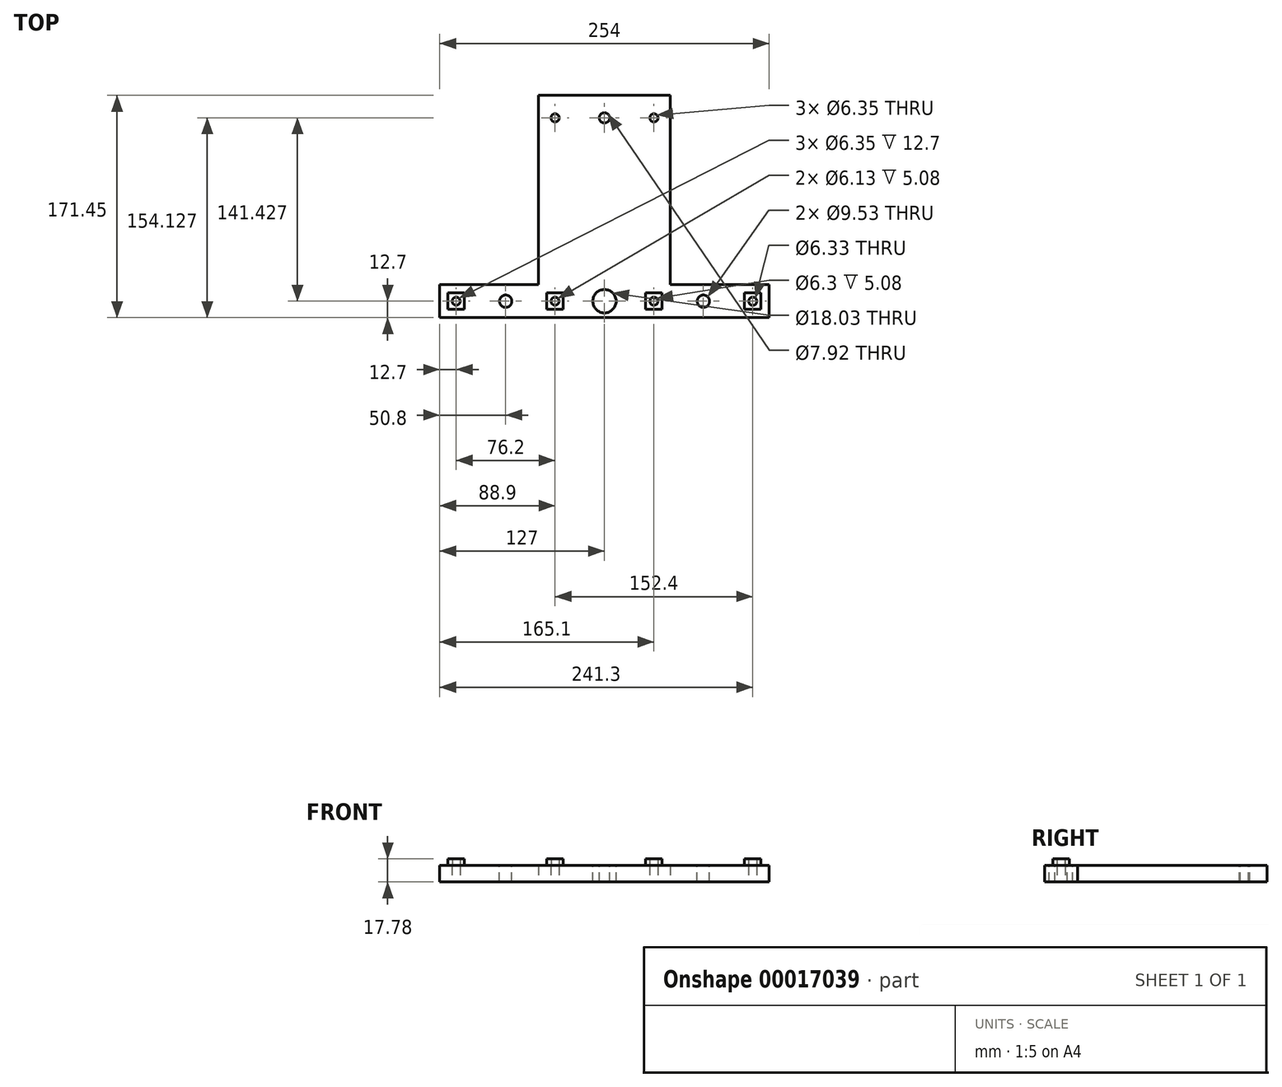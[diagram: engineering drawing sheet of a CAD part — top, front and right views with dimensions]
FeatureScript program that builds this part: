
annotation { "Feature Type Name" : "Feature", "Feature Type Description" : "" }
export const myFeature = defineFeature(function(context is Context, id is Id, definition is map)
    precondition{}
    {
        {
            var Q0;
            Q0=qCreatedBy(makeId("Top.planeOp"),FACE);
            var sketch = newSketch(context, id + "F0", { "sketchPlane" : qUnion([Q0])});
            skLineSegment(sketch, "E0.bottom", {"start": v(127, 12.7) * mm, "end": v(50.8, 12.7) * mm});
            skLineSegment(sketch, "E0.top", {"start": v(127, -12.7) * mm, "end": v(-127, -12.7) * mm});
            skLineSegment(sketch, "E0.left", {"start": v(127, 12.7) * mm, "end": v(127, -12.7) * mm});
            skLineSegment(sketch, "E0.right", {"start": v(-127, 12.7) * mm, "end": v(-127, -12.7) * mm});
            skPoint(sketch, "E0.middle", {"position": v(0, 0) * mm});
            skLineSegment(sketch, "E1.bottom", {"start": v(50.8, 158.75) * mm, "end": v(-50.8, 158.75) * mm});
            skLineSegment(sketch, "E1.top", {"start": v(50.8, -158.75) * mm, "end": v(-50.8, -158.75) * mm});
            skLineSegment(sketch, "E1.left", {"start": v(50.8, 158.75) * mm, "end": v(50.8, 12.7) * mm});
            skLineSegment(sketch, "E1.right", {"start": v(-50.8, 158.75) * mm, "end": v(-50.8, 12.7) * mm});
            skLineSegment(sketch, "E2.trimOffspring", {"start": v(-50.8, 12.7) * mm, "end": v(-127, 12.7) * mm});
            skCircle(sketch, "E3", {"center": v(114.3, 0) * mm, "radius": 3.18 * mm});
            skCircle(sketch, "E4", {"center": v(38.1, 0) * mm, "radius": 3.18 * mm});
            skCircle(sketch, "E5", {"center": v(-38.1, 0) * mm, "radius": 3.18 * mm});
            skCircle(sketch, "E6", {"center": v(-114.3, 0) * mm, "radius": 3.18 * mm});
            skSolve(sketch);
        }
        {
            var Q0;
            Q0 = qSketchRegion(id + "F0", true);
            extrude(context, id + "F1", {"entities" : qUnion([Q0]), "depth" : 12.7 * mm});
        }
        {
            var Q0;
            Q0=makeQuery(id+"F1.opExtrude","CAP_FACE",FACE,{"disambiguationData":[OSD([sQuery(id+"F0.wireOp",EDGE,"E0.bottom"),sQuery(id+"F0.wireOp",EDGE,"E0.top"),sQuery(id+"F0.wireOp",EDGE,"E0.left"),sQuery(id+"F0.wireOp",EDGE,"E0.right"),sQuery(id+"F0.wireOp",EDGE,"E1.bottom"),sQuery(id+"F0.wireOp",EDGE,"E1.left"),sQuery(id+"F0.wireOp",EDGE,"E1.right"),sQuery(id+"F0.wireOp",EDGE,"E2.trimOffspring"),sQuery(id+"F0.wireOp",EDGE,"E3"),sQuery(id+"F0.wireOp",EDGE,"E4"),sQuery(id+"F0.wireOp",EDGE,"E5"),sQuery(id+"F0.wireOp",EDGE,"E6")])],"isStart":false});
            var sketch = newSketch(context, id + "F2", { "sketchPlane" : qUnion([Q0])});
            skLineSegment(sketch, "E7.bottom", {"start": v(120.65, 6.35) * mm, "end": v(107.95, 6.35) * mm});
            skLineSegment(sketch, "E7.top", {"start": v(120.65, -6.35) * mm, "end": v(107.95, -6.35) * mm});
            skLineSegment(sketch, "E7.left", {"start": v(120.65, 6.35) * mm, "end": v(120.65, -6.35) * mm});
            skLineSegment(sketch, "E7.right", {"start": v(107.95, 6.35) * mm, "end": v(107.95, -6.35) * mm});
            skPoint(sketch, "E7.middle", {"position": v(114.3, 0) * mm});
            skLineSegment(sketch, "E8.bottom", {"start": v(44.45, 6.35) * mm, "end": v(31.75, 6.35) * mm});
            skLineSegment(sketch, "E8.top", {"start": v(44.45, -6.35) * mm, "end": v(31.75, -6.35) * mm});
            skLineSegment(sketch, "E8.left", {"start": v(44.45, 6.35) * mm, "end": v(44.45, -6.35) * mm});
            skLineSegment(sketch, "E8.right", {"start": v(31.75, 6.35) * mm, "end": v(31.75, -6.35) * mm});
            skPoint(sketch, "E8.middle", {"position": v(38.1, 0) * mm});
            skLineSegment(sketch, "E9.bottom", {"start": v(-31.75, 6.35) * mm, "end": v(-44.45, 6.35) * mm});
            skLineSegment(sketch, "E9.top", {"start": v(-31.75, -6.35) * mm, "end": v(-44.45, -6.35) * mm});
            skLineSegment(sketch, "E9.left", {"start": v(-31.75, 6.35) * mm, "end": v(-31.75, -6.35) * mm});
            skLineSegment(sketch, "E9.right", {"start": v(-44.45, 6.35) * mm, "end": v(-44.45, -6.35) * mm});
            skPoint(sketch, "E9.middle", {"position": v(-38.1, 0) * mm});
            skLineSegment(sketch, "E10.bottom", {"start": v(-107.95, 6.35) * mm, "end": v(-120.65, 6.35) * mm});
            skLineSegment(sketch, "E10.top", {"start": v(-107.95, -6.35) * mm, "end": v(-120.65, -6.35) * mm});
            skLineSegment(sketch, "E10.left", {"start": v(-107.95, 6.35) * mm, "end": v(-107.95, -6.35) * mm});
            skLineSegment(sketch, "E10.right", {"start": v(-120.65, 6.35) * mm, "end": v(-120.65, -6.35) * mm});
            skPoint(sketch, "E10.middle", {"position": v(-114.3, 0) * mm});
            skCircle(sketch, "E11", {"center": v(-114.3, 0) * mm, "radius": 3.07 * mm});
            skCircle(sketch, "E12", {"center": v(-38.1, 0) * mm, "radius": 3.07 * mm});
            skCircle(sketch, "E13", {"center": v(38.1, 0) * mm, "radius": 3.15 * mm});
            skCircle(sketch, "E14", {"center": v(114.3, 0) * mm, "radius": 3.17 * mm});
            skSolve(sketch);
        }
        {
            var Q0;
            Q0 = qSketchRegion(id + "F2", true);
            extrude(context, id + "F3", {"entities" : qUnion([Q0]), "operationType" : NewBodyOperationType.ADD, "depth" : 5.08 * mm});
        }
        {
            var Q0;
            Q0=makeQuery(id+"F1.opExtrude","CAP_FACE",FACE,{"disambiguationData":[OSD([sQuery(id+"F0.wireOp",EDGE,"E0.bottom"),sQuery(id+"F0.wireOp",EDGE,"E0.top"),sQuery(id+"F0.wireOp",EDGE,"E0.left"),sQuery(id+"F0.wireOp",EDGE,"E0.right"),sQuery(id+"F0.wireOp",EDGE,"E1.bottom"),sQuery(id+"F0.wireOp",EDGE,"E1.left"),sQuery(id+"F0.wireOp",EDGE,"E1.right"),sQuery(id+"F0.wireOp",EDGE,"E2.trimOffspring"),sQuery(id+"F0.wireOp",EDGE,"E3"),sQuery(id+"F0.wireOp",EDGE,"E4"),sQuery(id+"F0.wireOp",EDGE,"E5"),sQuery(id+"F0.wireOp",EDGE,"E6")])],"isStart":false});
            var sketch = newSketch(context, id + "F4", { "sketchPlane" : qUnion([Q0])});
            skCircle(sketch, "E15", {"center": v(0, 0) * mm, "radius": 9.02 * mm});
            skSolve(sketch);
        }
        {
            var Q0;
            Q0 = qSketchRegion(id + "F4", true);
            extrude(context, id + "F5", {"entities" : qUnion([Q0]), "operationType" : NewBodyOperationType.REMOVE, "oppositeDirection" : true, "depth" : 25.4 * mm});
        }
        {
            var Q0;
            Q0=makeQuery(id+"F1.opExtrude","CAP_FACE",FACE,{"disambiguationData":[OSD([sQuery(id+"F0.wireOp",EDGE,"E0.bottom"),sQuery(id+"F0.wireOp",EDGE,"E0.top"),sQuery(id+"F0.wireOp",EDGE,"E0.left"),sQuery(id+"F0.wireOp",EDGE,"E0.right"),sQuery(id+"F0.wireOp",EDGE,"E1.bottom"),sQuery(id+"F0.wireOp",EDGE,"E1.left"),sQuery(id+"F0.wireOp",EDGE,"E1.right"),sQuery(id+"F0.wireOp",EDGE,"E2.trimOffspring"),sQuery(id+"F0.wireOp",EDGE,"E3"),sQuery(id+"F0.wireOp",EDGE,"E4"),sQuery(id+"F0.wireOp",EDGE,"E5"),sQuery(id+"F0.wireOp",EDGE,"E6")])],"isStart":false});
            var sketch = newSketch(context, id + "F6", { "sketchPlane" : qUnion([Q0])});
            skCircle(sketch, "E16", {"center": v(-76.2, 0) * mm, "radius": 4.76 * mm});
            skCircle(sketch, "E17", {"center": v(76.2, 0) * mm, "radius": 4.76 * mm});
            skSolve(sketch);
        }
        {
            var Q0;
            Q0 = qSketchRegion(id + "F6", true);
            extrude(context, id + "F7", {"entities" : qUnion([Q0]), "operationType" : NewBodyOperationType.REMOVE, "oppositeDirection" : true, "depth" : 25.4 * mm});
        }
        {
            var Q0;
            Q0=makeQuery(id+"F1.opExtrude","CAP_FACE",FACE,{"disambiguationData":[OSD([sQuery(id+"F0.wireOp",EDGE,"E0.bottom"),sQuery(id+"F0.wireOp",EDGE,"E0.top"),sQuery(id+"F0.wireOp",EDGE,"E0.left"),sQuery(id+"F0.wireOp",EDGE,"E0.right"),sQuery(id+"F0.wireOp",EDGE,"E1.bottom"),sQuery(id+"F0.wireOp",EDGE,"E1.left"),sQuery(id+"F0.wireOp",EDGE,"E1.right"),sQuery(id+"F0.wireOp",EDGE,"E2.trimOffspring"),sQuery(id+"F0.wireOp",EDGE,"E3"),sQuery(id+"F0.wireOp",EDGE,"E4"),sQuery(id+"F0.wireOp",EDGE,"E5"),sQuery(id+"F0.wireOp",EDGE,"E6")])],"isStart":false});
            var sketch = newSketch(context, id + "F8", { "sketchPlane" : qUnion([Q0])});
            skCircle(sketch, "E18", {"center": v(-38.1, 141.43) * mm, "radius": 3.18 * mm});
            skCircle(sketch, "E19", {"center": v(38.1, 141.43) * mm, "radius": 3.18 * mm});
            skCircle(sketch, "E20", {"center": v(0, 141.43) * mm, "radius": 3.96 * mm});
            skSolve(sketch);
        }
        {
            var Q0;
            Q0 = qSketchRegion(id + "F8", true);
            extrude(context, id + "F9", {"entities" : qUnion([Q0]), "operationType" : NewBodyOperationType.REMOVE, "endBound" : BoundingType.THROUGH_ALL, "oppositeDirection" : true, "depth" : 25.4 * mm});
        }
        {
            var Q0;
            Q0 = qSketchRegion(id + "F8", true);
            extrude(context, id + "F10", {"entities" : qUnion([Q0]), "operationType" : NewBodyOperationType.REMOVE, "endBound" : BoundingType.THROUGH_ALL, "oppositeDirection" : true, "depth" : 25.4 * mm});
        }
    });
